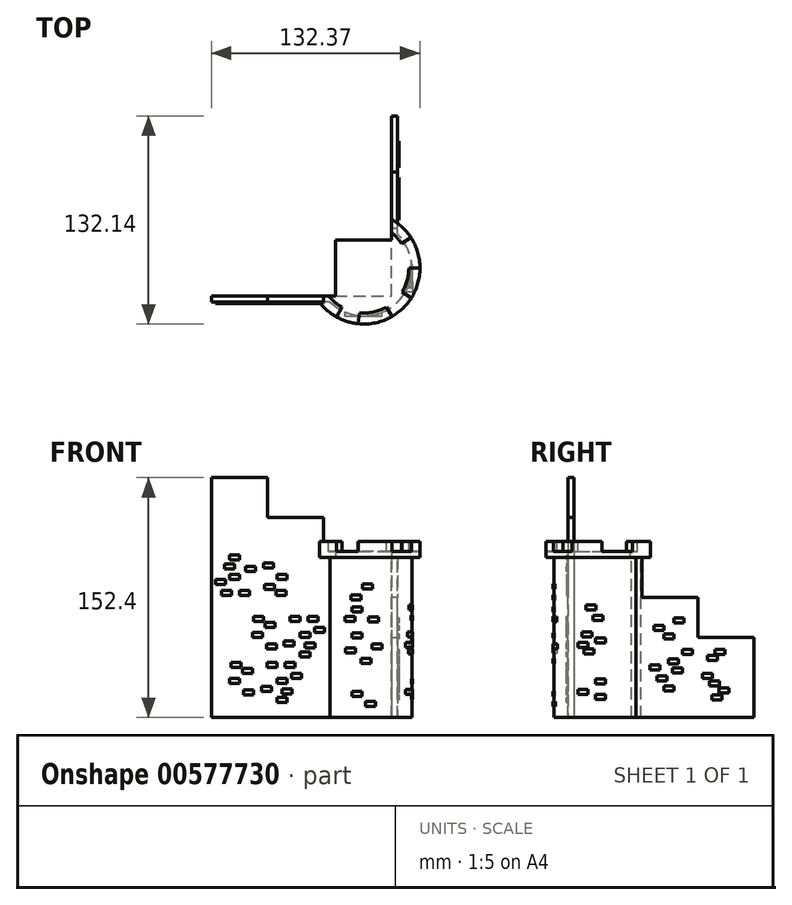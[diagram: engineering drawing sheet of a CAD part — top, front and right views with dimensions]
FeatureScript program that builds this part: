
annotation { "Feature Type Name" : "Feature", "Feature Type Description" : "" }
export const myFeature = defineFeature(function(context is Context, id is Id, definition is map)
    precondition{}
    {
        {
            var Q0;
            Q0=qCreatedBy(makeId("Top.planeOp"),FACE);
            var sketch = newSketch(context, id + "F0", { "sketchPlane" : qUnion([Q0])});
            skLineSegment(sketch, "E0.bottom", {"start": v(-57.15, -57.15) * mm, "end": v(57.15, -57.15) * mm});
            skLineSegment(sketch, "E0.top", {"start": v(-57.15, 57.15) * mm, "end": v(57.15, 57.15) * mm});
            skLineSegment(sketch, "E0.left", {"start": v(-57.15, -57.15) * mm, "end": v(-57.15, 57.15) * mm});
            skLineSegment(sketch, "E0.right", {"start": v(57.15, -57.15) * mm, "end": v(57.15, 57.15) * mm});
            skPoint(sketch, "E0.middle", {"position": v(0, 0) * mm});
            skLineSegment(sketch, "E1.bottom", {"start": v(57.15, -57.15) * mm, "end": v(21.6, -57.15) * mm});
            skLineSegment(sketch, "E1.top", {"start": v(57.15, -21.59) * mm, "end": v(21.59, -21.6) * mm});
            skLineSegment(sketch, "E1.left", {"start": v(57.15, -57.15) * mm, "end": v(57.15, -21.59) * mm});
            skLineSegment(sketch, "E1.right", {"start": v(21.6, -57.15) * mm, "end": v(21.59, -21.6) * mm});
            skLineSegment(sketch, "E2.bottom", {"start": v(57.15, -57.15) * mm, "end": v(39.37, -57.15) * mm});
            skLineSegment(sketch, "E2.top", {"start": v(57.15, -39.37) * mm, "end": v(39.37, -39.37) * mm});
            skLineSegment(sketch, "E2.left", {"start": v(57.15, -57.15) * mm, "end": v(57.15, -39.37) * mm});
            skLineSegment(sketch, "E2.right", {"start": v(39.37, -57.15) * mm, "end": v(39.37, -39.37) * mm});
            skSolve(sketch);
        }
        {
            var Q0;
            Q0=qCreatedBy(makeId("Top.planeOp"),FACE);
            var sketch = newSketch(context, id + "F1", { "sketchPlane" : qUnion([Q0])});
            skLineSegment(sketch, "E3.bottom", {"start": v(57.14, -57.15) * mm, "end": v(-57.16, -57.15) * mm});
            skLineSegment(sketch, "E3.top", {"start": v(57.14, -60.96) * mm, "end": v(-57.16, -60.96) * mm});
            skLineSegment(sketch, "E3.left", {"start": v(57.14, -57.15) * mm, "end": v(57.14, -60.96) * mm});
            skLineSegment(sketch, "E3.right", {"start": v(-57.16, -57.15) * mm, "end": v(-57.16, -60.96) * mm});
            skLineSegment(sketch, "E4.bottom", {"start": v(57.14, -60.96) * mm, "end": v(60.95, -60.96) * mm});
            skLineSegment(sketch, "E4.top", {"start": v(57.14, 57.15) * mm, "end": v(60.95, 57.15) * mm});
            skLineSegment(sketch, "E4.left", {"start": v(57.14, -60.96) * mm, "end": v(57.14, 57.15) * mm});
            skLineSegment(sketch, "E4.right", {"start": v(60.95, -60.96) * mm, "end": v(60.95, 57.15) * mm});
            skSolve(sketch);
        }
        {
            var Q0;
            Q0=qSketchRegion(id+"F1",true);
            extrude(context, id + "F2", {"entities" : qUnion([Q0]), "depth" : 152.4 * mm, "offsetDistance" : 25.4 * mm});
        }
        {
            var Q0;
            Q0=makeQuery(id+"F2.opExtrude","CAP_FACE",FACE,{"disambiguationData":[OSD([sQuery(id+"F1.wireOp",EDGE,"E3.bottom"),sQuery(id+"F1.wireOp",EDGE,"E3.top"),sQuery(id+"F1.wireOp",EDGE,"E3.right"),sQuery(id+"F1.wireOp",EDGE,"E4.bottom"),sQuery(id+"F1.wireOp",EDGE,"E4.top"),sQuery(id+"F1.wireOp",EDGE,"E4.left"),sQuery(id+"F1.wireOp",EDGE,"E4.right")])],"isStart":false});
            var sketch = newSketch(context, id + "F3", { "sketchPlane" : qUnion([Q0])});
            skLineSegment(sketch, "E5.bottom", {"start": v(-57.16, -60.96) * mm, "end": v(-21.56, -60.96) * mm});
            skLineSegment(sketch, "E5.top", {"start": v(-57.16, -57.15) * mm, "end": v(-21.56, -57.15) * mm});
            skLineSegment(sketch, "E5.left", {"start": v(-57.16, -60.96) * mm, "end": v(-57.16, -57.15) * mm});
            skLineSegment(sketch, "E5.right", {"start": v(-21.56, -60.96) * mm, "end": v(-21.56, -57.15) * mm});
            skSolve(sketch);
        }
        {
            var Q0;
            {var subQ2=sQuery(id+"F3.wireOp",EDGE,"E5.right");Q0=makeQuery(id+"F3.imprint","IMPRINT",FACE,{"disambiguationData":[TD([[makeQuery(id+"F3.imprint","IMPRINT",EDGE,{"derivedFrom":subQ2}),-1.0]])]});}
            var sketch = newSketch(context, id + "F4", { "sketchPlane" : qUnion([Q0])});
            skLineSegment(sketch, "E6.bottom", {"start": v(-21.56, -60.96) * mm, "end": v(13.98, -60.96) * mm});
            skLineSegment(sketch, "E6.top", {"start": v(-21.56, -57.15) * mm, "end": v(13.98, -57.15) * mm});
            skLineSegment(sketch, "E6.left", {"start": v(-21.56, -60.96) * mm, "end": v(-21.56, -57.15) * mm});
            skLineSegment(sketch, "E6.right", {"start": v(13.98, -60.96) * mm, "end": v(13.98, -57.15) * mm});
            skSolve(sketch);
        }
        {
            var Q0;
            {var subQ2=sQuery(id+"F3.wireOp",EDGE,"E5.right");Q0=makeQuery(id+"F3.imprint","IMPRINT",FACE,{"disambiguationData":[TD([[makeQuery(id+"F3.imprint","IMPRINT",EDGE,{"derivedFrom":subQ2}),-1.0]])]});}
            var sketch = newSketch(context, id + "F5", { "sketchPlane" : qUnion([Q0])});
            skLineSegment(sketch, "E7.bottom", {"start": v(60.94, 57.16) * mm, "end": v(57.04, 57.16) * mm});
            skLineSegment(sketch, "E7.top", {"start": v(60.94, 21.5) * mm, "end": v(57.04, 21.5) * mm});
            skLineSegment(sketch, "E7.left", {"start": v(60.94, 57.16) * mm, "end": v(60.94, 21.5) * mm});
            skLineSegment(sketch, "E7.right", {"start": v(57.04, 57.16) * mm, "end": v(57.04, 21.5) * mm});
            skSolve(sketch);
        }
        {
            var Q0;
            {var subQ2=sQuery(id+"F3.wireOp",EDGE,"E5.right");Q0=makeQuery(id+"F3.imprint","IMPRINT",FACE,{"disambiguationData":[TD([[makeQuery(id+"F3.imprint","IMPRINT",EDGE,{"derivedFrom":subQ2}),-1.0]])]});}
            var sketch = newSketch(context, id + "F6", { "sketchPlane" : qUnion([Q0])});
            skLineSegment(sketch, "E8.bottom", {"start": v(61.03, 21.57) * mm, "end": v(56.87, 21.57) * mm});
            skLineSegment(sketch, "E8.top", {"start": v(61.03, -14) * mm, "end": v(56.87, -14) * mm});
            skLineSegment(sketch, "E8.left", {"start": v(61.03, 21.57) * mm, "end": v(61.03, -14) * mm});
            skLineSegment(sketch, "E8.right", {"start": v(56.87, 21.57) * mm, "end": v(56.87, -14) * mm});
            skSolve(sketch);
        }
        {
            var Q0;
            Q0=qSketchRegion(id+"F4",true);
            extrude(context, id + "F7", {"entities" : qUnion([Q0]), "operationType" : NewBodyOperationType.REMOVE, "oppositeDirection" : true, "depth" : 25.4 * mm, "offsetDistance" : 25.4 * mm});
        }
        {
            var Q0;
            Q0=qSketchRegion(id+"F6",true);
            extrude(context, id + "F8", {"entities" : qUnion([Q0]), "operationType" : NewBodyOperationType.REMOVE, "oppositeDirection" : true, "depth" : 76.2 * mm, "offsetDistance" : 25.4 * mm});
        }
        {
            var Q0;
            {var subQ2=sQuery(id+"F3.wireOp",EDGE,"E5.right");Q0=makeQuery(id+"F3.imprint","IMPRINT",FACE,{"disambiguationData":[TD([[makeQuery(id+"F3.imprint","IMPRINT",EDGE,{"derivedFrom":subQ2}),-1.0]])]});}
            var sketch = newSketch(context, id + "F9", { "sketchPlane" : qUnion([Q0])});
            skLineSegment(sketch, "E9.bottom", {"start": v(13.92, -61.53) * mm, "end": v(78.38, -61.53) * mm});
            skLineSegment(sketch, "E9.top", {"start": v(13.92, -13.89) * mm, "end": v(78.38, -13.89) * mm});
            skLineSegment(sketch, "E9.left", {"start": v(13.92, -61.53) * mm, "end": v(13.92, -13.89) * mm});
            skLineSegment(sketch, "E9.right", {"start": v(78.38, -61.53) * mm, "end": v(78.38, -13.89) * mm});
            skSolve(sketch);
        }
        {
            var Q0;
            Q0=qSketchRegion(id+"F9",true);
            extrude(context, id + "F10", {"entities" : qUnion([Q0]), "operationType" : NewBodyOperationType.REMOVE, "oppositeDirection" : true, "depth" : 50.8 * mm, "offsetDistance" : 25.4 * mm});
        }
        {
            var Q0;
            Q0=makeQuery(id+"F10.boolean.opBoolean","COPY",FACE,{"derivedFrom":makeQuery(id+"F10.opExtrude","CAP_FACE",FACE,{"disambiguationData":[OSD([sQuery(id+"F9.wireOp",EDGE,"E9.bottom"),sQuery(id+"F9.wireOp",EDGE,"E9.top"),sQuery(id+"F9.wireOp",EDGE,"E9.left"),sQuery(id+"F9.wireOp",EDGE,"E9.right")])],"isStart":false})});
            var sketch = newSketch(context, id + "F11", { "sketchPlane" : qUnion([Q0])});
            skCircle(sketch, "E10", {"center": v(39.65, -39.43) * mm, "radius": 35.56 * mm});
            skSolve(sketch);
        }
        {
            var Q0;
            Q0=qSketchRegion(id+"F11",true);
            extrude(context, id + "F12", {"entities" : qUnion([Q0]), "operationType" : NewBodyOperationType.ADD, "depth" : 10.16 * mm, "offsetDistance" : 25.4 * mm});
        }
        {
            var Q0;
            Q0=qSketchRegion(id+"F5",true);
            extrude(context, id + "F13", {"entities" : qUnion([Q0]), "operationType" : NewBodyOperationType.REMOVE, "oppositeDirection" : true, "depth" : 101.6 * mm, "offsetDistance" : 25.4 * mm});
        }
        {
            var Q0;
            Q0=makeQuery(id+"F12.opExtrude","CAP_FACE",FACE,{"disambiguationData":[OSD([sQuery(id+"F11.wireOp",EDGE,"E10")])],"isStart":true});
            var sketch = newSketch(context, id + "F14", { "sketchPlane" : qUnion([Q0])});
            skCircle(sketch, "E11", {"center": v(39.65, 39.43) * mm, "radius": 30.4 * mm});
            skSolve(sketch);
        }
        {
            var Q0;
            Q0=qSketchRegion(id+"F14",true);
            extrude(context, id + "F15", {"entities" : qUnion([Q0]), "operationType" : NewBodyOperationType.ADD, "depth" : 101.6 * mm, "offsetDistance" : 25.4 * mm});
        }
        {
            var Q0;
            Q0=makeQuery(id+"F2.opExtrude","SWEPT_FACE",FACE,{"disambiguationData":[OSD([sQuery(id+"F1.wireOp",EDGE,"E3.top"),sQuery(id+"F1.wireOp",EDGE,"E4.bottom")])]});
            var sketch = newSketch(context, id + "F16", { "sketchPlane" : qUnion([Q0])});
            skLineSegment(sketch, "E12.bottom", {"start": v(-45.66, 21.63) * mm, "end": v(-39.31, 21.63) * mm});
            skLineSegment(sketch, "E12.top", {"start": v(-45.66, 24.8) * mm, "end": v(-39.31, 24.8) * mm});
            skLineSegment(sketch, "E12.left", {"start": v(-45.66, 21.63) * mm, "end": v(-45.66, 24.8) * mm});
            skLineSegment(sketch, "E12.right", {"start": v(-39.31, 21.63) * mm, "end": v(-39.31, 24.8) * mm});
            skLineSegment(sketch, "E13.bottom", {"start": v(-6.35, 24.8) * mm, "end": v(0, 24.8) * mm});
            skLineSegment(sketch, "E13.top", {"start": v(-6.35, 27.98) * mm, "end": v(0, 27.98) * mm});
            skLineSegment(sketch, "E13.left", {"start": v(-6.35, 24.8) * mm, "end": v(-6.35, 27.98) * mm});
            skLineSegment(sketch, "E13.right", {"start": v(0, 24.8) * mm, "end": v(0, 27.98) * mm});
            skLineSegment(sketch, "E14.bottom", {"start": v(-25.42, 19.65) * mm, "end": v(-19.07, 19.65) * mm});
            skLineSegment(sketch, "E14.top", {"start": v(-25.42, 16.47) * mm, "end": v(-19.07, 16.47) * mm});
            skLineSegment(sketch, "E14.left", {"start": v(-25.42, 19.65) * mm, "end": v(-25.42, 16.47) * mm});
            skLineSegment(sketch, "E14.right", {"start": v(-19.07, 19.65) * mm, "end": v(-19.07, 16.47) * mm});
            skLineSegment(sketch, "E15.bottom", {"start": v(-38.5, 31.94) * mm, "end": v(-44.85, 31.94) * mm});
            skLineSegment(sketch, "E15.top", {"start": v(-38.5, 35.11) * mm, "end": v(-44.85, 35.11) * mm});
            skLineSegment(sketch, "E15.left", {"start": v(-38.5, 31.94) * mm, "end": v(-38.5, 35.11) * mm});
            skLineSegment(sketch, "E15.right", {"start": v(-44.85, 31.94) * mm, "end": v(-44.85, 35.11) * mm});
            skLineSegment(sketch, "E16.bottom", {"start": v(-31.2, 27.98) * mm, "end": v(-37.54, 27.98) * mm});
            skLineSegment(sketch, "E16.top", {"start": v(-31.2, 31.15) * mm, "end": v(-37.54, 31.15) * mm});
            skLineSegment(sketch, "E16.left", {"start": v(-31.2, 27.98) * mm, "end": v(-31.2, 31.15) * mm});
            skLineSegment(sketch, "E16.right", {"start": v(-37.54, 27.98) * mm, "end": v(-37.54, 31.15) * mm});
            skLineSegment(sketch, "E17.bottom", {"start": v(-10.36, 31.94) * mm, "end": v(-4, 31.94) * mm});
            skLineSegment(sketch, "E17.top", {"start": v(-10.36, 35.11) * mm, "end": v(-4, 35.11) * mm});
            skLineSegment(sketch, "E17.left", {"start": v(-10.36, 31.94) * mm, "end": v(-10.36, 35.11) * mm});
            skLineSegment(sketch, "E17.right", {"start": v(-4, 31.94) * mm, "end": v(-4, 35.11) * mm});
            skLineSegment(sketch, "E18.bottom", {"start": v(-30.45, 14.43) * mm, "end": v(-36.8, 14.43) * mm});
            skLineSegment(sketch, "E18.top", {"start": v(-30.45, 17.6) * mm, "end": v(-36.8, 17.6) * mm});
            skLineSegment(sketch, "E18.left", {"start": v(-30.45, 14.43) * mm, "end": v(-30.45, 17.6) * mm});
            skLineSegment(sketch, "E18.right", {"start": v(-36.8, 14.43) * mm, "end": v(-36.8, 17.6) * mm});
            skLineSegment(sketch, "E19.bottom", {"start": v(-15.4, 9.44) * mm, "end": v(-9.05, 9.44) * mm});
            skLineSegment(sketch, "E19.top", {"start": v(-15.4, 12.62) * mm, "end": v(-9.05, 12.62) * mm});
            skLineSegment(sketch, "E19.left", {"start": v(-15.4, 9.44) * mm, "end": v(-15.4, 12.62) * mm});
            skLineSegment(sketch, "E19.right", {"start": v(-9.05, 9.44) * mm, "end": v(-9.05, 12.62) * mm});
            skLineSegment(sketch, "E20.bottom", {"start": v(-12.27, 15.05) * mm, "end": v(-5.92, 15.05) * mm});
            skLineSegment(sketch, "E20.top", {"start": v(-12.27, 18.22) * mm, "end": v(-5.92, 18.22) * mm});
            skLineSegment(sketch, "E20.left", {"start": v(-12.27, 15.05) * mm, "end": v(-12.27, 18.22) * mm});
            skLineSegment(sketch, "E20.right", {"start": v(-5.92, 15.05) * mm, "end": v(-5.92, 18.22) * mm});
            skPoint(sketch, "E21.firstSnap0", {"position": v(-9.1, 15.05) * mm});
            skLineSegment(sketch, "E21.bottom", {"start": v(-9.1, 21.63) * mm, "end": v(-15.44, 21.63) * mm});
            skLineSegment(sketch, "E21.top", {"start": v(-9.1, 24.8) * mm, "end": v(-15.44, 24.8) * mm});
            skLineSegment(sketch, "E21.left", {"start": v(-9.1, 21.63) * mm, "end": v(-9.1, 24.8) * mm});
            skLineSegment(sketch, "E21.right", {"start": v(-15.44, 21.63) * mm, "end": v(-15.44, 24.8) * mm});
            skLineSegment(sketch, "E22.bottom", {"start": v(-15.44, 31.94) * mm, "end": v(-21.8, 31.94) * mm});
            skLineSegment(sketch, "E22.top", {"start": v(-15.44, 35.11) * mm, "end": v(-21.8, 35.11) * mm});
            skLineSegment(sketch, "E22.left", {"start": v(-15.44, 31.94) * mm, "end": v(-15.44, 35.11) * mm});
            skLineSegment(sketch, "E22.right", {"start": v(-21.8, 31.94) * mm, "end": v(-21.8, 35.11) * mm});
            skLineSegment(sketch, "E23.bottom", {"start": v(-31.2, 50.73) * mm, "end": v(-24.84, 50.73) * mm});
            skLineSegment(sketch, "E23.top", {"start": v(-31.2, 53.9) * mm, "end": v(-24.84, 53.9) * mm});
            skLineSegment(sketch, "E23.left", {"start": v(-31.2, 50.73) * mm, "end": v(-31.2, 53.9) * mm});
            skLineSegment(sketch, "E23.right", {"start": v(-24.84, 50.73) * mm, "end": v(-24.84, 53.9) * mm});
            skLineSegment(sketch, "E24.bottom", {"start": v(8.12, 53.9) * mm, "end": v(14.47, 53.9) * mm});
            skLineSegment(sketch, "E24.top", {"start": v(8.12, 57.08) * mm, "end": v(14.47, 57.08) * mm});
            skLineSegment(sketch, "E24.left", {"start": v(8.12, 53.9) * mm, "end": v(8.12, 57.08) * mm});
            skLineSegment(sketch, "E24.right", {"start": v(14.47, 53.9) * mm, "end": v(14.47, 57.08) * mm});
            skLineSegment(sketch, "E25.bottom", {"start": v(-10.95, 48.75) * mm, "end": v(-4.6, 48.75) * mm});
            skLineSegment(sketch, "E25.top", {"start": v(-10.95, 45.57) * mm, "end": v(-4.6, 45.57) * mm});
            skLineSegment(sketch, "E25.left", {"start": v(-10.95, 48.75) * mm, "end": v(-10.95, 45.57) * mm});
            skLineSegment(sketch, "E25.right", {"start": v(-4.6, 48.75) * mm, "end": v(-4.6, 45.57) * mm});
            skLineSegment(sketch, "E26.bottom", {"start": v(-24.03, 61.04) * mm, "end": v(-30.38, 61.04) * mm});
            skLineSegment(sketch, "E26.top", {"start": v(-24.03, 64.21) * mm, "end": v(-30.38, 64.21) * mm});
            skLineSegment(sketch, "E26.left", {"start": v(-24.03, 61.04) * mm, "end": v(-24.03, 64.21) * mm});
            skLineSegment(sketch, "E26.right", {"start": v(-30.38, 61.04) * mm, "end": v(-30.38, 64.21) * mm});
            skLineSegment(sketch, "E27.bottom", {"start": v(-16.72, 57.08) * mm, "end": v(-23.07, 57.08) * mm});
            skLineSegment(sketch, "E27.top", {"start": v(-16.72, 60.25) * mm, "end": v(-23.07, 60.25) * mm});
            skLineSegment(sketch, "E27.left", {"start": v(-16.72, 57.08) * mm, "end": v(-16.72, 60.25) * mm});
            skLineSegment(sketch, "E27.right", {"start": v(-23.07, 57.08) * mm, "end": v(-23.07, 60.25) * mm});
            skLineSegment(sketch, "E28.bottom", {"start": v(4.11, 61.04) * mm, "end": v(10.46, 61.04) * mm});
            skLineSegment(sketch, "E28.top", {"start": v(4.11, 64.21) * mm, "end": v(10.46, 64.21) * mm});
            skLineSegment(sketch, "E28.left", {"start": v(4.11, 61.04) * mm, "end": v(4.11, 64.21) * mm});
            skLineSegment(sketch, "E28.right", {"start": v(10.46, 61.04) * mm, "end": v(10.46, 64.21) * mm});
            skLineSegment(sketch, "E29.bottom", {"start": v(-15.98, 43.53) * mm, "end": v(-22.33, 43.53) * mm});
            skLineSegment(sketch, "E29.top", {"start": v(-15.98, 46.7) * mm, "end": v(-22.33, 46.7) * mm});
            skLineSegment(sketch, "E29.left", {"start": v(-15.98, 43.53) * mm, "end": v(-15.98, 46.7) * mm});
            skLineSegment(sketch, "E29.right", {"start": v(-22.33, 43.53) * mm, "end": v(-22.33, 46.7) * mm});
            skLineSegment(sketch, "E30.bottom", {"start": v(-0.93, 38.54) * mm, "end": v(5.42, 38.54) * mm});
            skLineSegment(sketch, "E30.top", {"start": v(-0.93, 41.72) * mm, "end": v(5.42, 41.72) * mm});
            skLineSegment(sketch, "E30.left", {"start": v(-0.93, 38.54) * mm, "end": v(-0.93, 41.72) * mm});
            skLineSegment(sketch, "E30.right", {"start": v(5.42, 38.54) * mm, "end": v(5.42, 41.72) * mm});
            skLineSegment(sketch, "E31.bottom", {"start": v(2.2, 44.15) * mm, "end": v(8.55, 44.15) * mm});
            skLineSegment(sketch, "E31.top", {"start": v(2.2, 47.32) * mm, "end": v(8.55, 47.32) * mm});
            skLineSegment(sketch, "E31.left", {"start": v(2.2, 44.15) * mm, "end": v(2.2, 47.32) * mm});
            skLineSegment(sketch, "E31.right", {"start": v(8.55, 44.15) * mm, "end": v(8.55, 47.32) * mm});
            skPoint(sketch, "E32.firstSnap0", {"position": v(5.38, 44.15) * mm});
            skLineSegment(sketch, "E32.bottom", {"start": v(5.38, 50.73) * mm, "end": v(-0.97, 50.73) * mm});
            skLineSegment(sketch, "E32.top", {"start": v(5.38, 53.9) * mm, "end": v(-0.97, 53.9) * mm});
            skLineSegment(sketch, "E32.left", {"start": v(5.38, 50.73) * mm, "end": v(5.38, 53.9) * mm});
            skLineSegment(sketch, "E32.right", {"start": v(-0.97, 50.73) * mm, "end": v(-0.97, 53.9) * mm});
            skLineSegment(sketch, "E33.bottom", {"start": v(-0.97, 61.04) * mm, "end": v(-7.32, 61.04) * mm});
            skLineSegment(sketch, "E33.top", {"start": v(-0.97, 64.21) * mm, "end": v(-7.32, 64.21) * mm});
            skLineSegment(sketch, "E33.left", {"start": v(-0.97, 61.04) * mm, "end": v(-0.97, 64.21) * mm});
            skLineSegment(sketch, "E33.right", {"start": v(-7.32, 61.04) * mm, "end": v(-7.32, 64.21) * mm});
            skLineSegment(sketch, "E34.bottom", {"start": v(-9.05, 90.93) * mm, "end": v(-15.4, 90.93) * mm});
            skLineSegment(sketch, "E34.top", {"start": v(-9.05, 87.76) * mm, "end": v(-15.4, 87.76) * mm});
            skLineSegment(sketch, "E34.left", {"start": v(-9.05, 90.93) * mm, "end": v(-9.05, 87.76) * mm});
            skLineSegment(sketch, "E34.right", {"start": v(-15.4, 90.93) * mm, "end": v(-15.4, 87.76) * mm});
            skLineSegment(sketch, "E35.bottom", {"start": v(-48.36, 87.76) * mm, "end": v(-54.71, 87.76) * mm});
            skLineSegment(sketch, "E35.top", {"start": v(-48.36, 84.58) * mm, "end": v(-54.71, 84.58) * mm});
            skLineSegment(sketch, "E35.left", {"start": v(-48.36, 87.76) * mm, "end": v(-48.36, 84.58) * mm});
            skLineSegment(sketch, "E35.right", {"start": v(-54.71, 87.76) * mm, "end": v(-54.71, 84.58) * mm});
            skLineSegment(sketch, "E36.bottom", {"start": v(-29.3, 92.91) * mm, "end": v(-35.64, 92.91) * mm});
            skLineSegment(sketch, "E36.top", {"start": v(-29.3, 96.09) * mm, "end": v(-35.64, 96.09) * mm});
            skLineSegment(sketch, "E36.left", {"start": v(-29.3, 92.91) * mm, "end": v(-29.3, 96.09) * mm});
            skLineSegment(sketch, "E36.right", {"start": v(-35.64, 92.91) * mm, "end": v(-35.64, 96.09) * mm});
            skLineSegment(sketch, "E37.bottom", {"start": v(-16.22, 80.62) * mm, "end": v(-9.87, 80.62) * mm});
            skLineSegment(sketch, "E37.top", {"start": v(-16.22, 77.45) * mm, "end": v(-9.87, 77.45) * mm});
            skLineSegment(sketch, "E37.left", {"start": v(-16.22, 80.62) * mm, "end": v(-16.22, 77.45) * mm});
            skLineSegment(sketch, "E37.right", {"start": v(-9.87, 80.62) * mm, "end": v(-9.87, 77.45) * mm});
            skLineSegment(sketch, "E38.bottom", {"start": v(-23.52, 84.58) * mm, "end": v(-17.17, 84.58) * mm});
            skLineSegment(sketch, "E38.top", {"start": v(-23.52, 81.4) * mm, "end": v(-17.17, 81.4) * mm});
            skLineSegment(sketch, "E38.left", {"start": v(-23.52, 84.58) * mm, "end": v(-23.52, 81.4) * mm});
            skLineSegment(sketch, "E38.right", {"start": v(-17.17, 84.58) * mm, "end": v(-17.17, 81.4) * mm});
            skLineSegment(sketch, "E39.bottom", {"start": v(-44.36, 80.62) * mm, "end": v(-50.7, 80.62) * mm});
            skLineSegment(sketch, "E39.top", {"start": v(-44.36, 77.45) * mm, "end": v(-50.7, 77.45) * mm});
            skLineSegment(sketch, "E39.left", {"start": v(-44.36, 80.62) * mm, "end": v(-44.36, 77.45) * mm});
            skLineSegment(sketch, "E39.right", {"start": v(-50.7, 80.62) * mm, "end": v(-50.7, 77.45) * mm});
            skLineSegment(sketch, "E40.bottom", {"start": v(-24.27, 98.13) * mm, "end": v(-17.92, 98.13) * mm});
            skLineSegment(sketch, "E40.top", {"start": v(-24.27, 94.95) * mm, "end": v(-17.92, 94.95) * mm});
            skLineSegment(sketch, "E40.left", {"start": v(-24.27, 98.13) * mm, "end": v(-24.27, 94.95) * mm});
            skLineSegment(sketch, "E40.right", {"start": v(-17.92, 98.13) * mm, "end": v(-17.92, 94.95) * mm});
            skLineSegment(sketch, "E41.bottom", {"start": v(-39.31, 103.12) * mm, "end": v(-45.66, 103.12) * mm});
            skLineSegment(sketch, "E41.top", {"start": v(-39.31, 99.94) * mm, "end": v(-45.66, 99.94) * mm});
            skLineSegment(sketch, "E41.left", {"start": v(-39.31, 103.12) * mm, "end": v(-39.31, 99.94) * mm});
            skLineSegment(sketch, "E41.right", {"start": v(-45.66, 103.12) * mm, "end": v(-45.66, 99.94) * mm});
            skLineSegment(sketch, "E42.bottom", {"start": v(-42.45, 97.51) * mm, "end": v(-48.8, 97.51) * mm});
            skLineSegment(sketch, "E42.top", {"start": v(-42.45, 94.34) * mm, "end": v(-48.8, 94.34) * mm});
            skLineSegment(sketch, "E42.left", {"start": v(-42.45, 97.51) * mm, "end": v(-42.45, 94.34) * mm});
            skLineSegment(sketch, "E42.right", {"start": v(-48.8, 97.51) * mm, "end": v(-48.8, 94.34) * mm});
            skPoint(sketch, "E43.firstSnap0", {"position": v(-45.62, 97.51) * mm});
            skLineSegment(sketch, "E43.bottom", {"start": v(-45.62, 90.93) * mm, "end": v(-39.27, 90.93) * mm});
            skLineSegment(sketch, "E43.top", {"start": v(-45.62, 87.76) * mm, "end": v(-39.27, 87.76) * mm});
            skLineSegment(sketch, "E43.left", {"start": v(-45.62, 90.93) * mm, "end": v(-45.62, 87.76) * mm});
            skLineSegment(sketch, "E43.right", {"start": v(-39.27, 90.93) * mm, "end": v(-39.27, 87.76) * mm});
            skLineSegment(sketch, "E44.bottom", {"start": v(-39.27, 80.62) * mm, "end": v(-32.92, 80.62) * mm});
            skLineSegment(sketch, "E44.top", {"start": v(-39.27, 77.45) * mm, "end": v(-32.92, 77.45) * mm});
            skLineSegment(sketch, "E44.left", {"start": v(-39.27, 80.62) * mm, "end": v(-39.27, 77.45) * mm});
            skLineSegment(sketch, "E44.right", {"start": v(-32.92, 80.62) * mm, "end": v(-32.92, 77.45) * mm});
            skSolve(sketch);
        }
        {
            var Q0;
            Q0 = qSketchRegion(id + "F16", true);
            extrude(context, id + "F17", {"entities" : qUnion([Q0]), "operationType" : NewBodyOperationType.ADD, "depth" : 1.02 * mm, "offsetDistance" : 25.4 * mm});
        }
        {
            var Q0;
            Q0=makeQuery(id+"F0.imprint","IMPRINT",FACE,{"disambiguationData":[TD([[makeQuery(id+"F0.imprint","IMPRINT",EDGE,{"derivedFrom":sQuery(id+"F0.wireOp",EDGE,"E0.bottom")}),1.0]])]});
            var sketch = newSketch(context, id + "F18", { "sketchPlane" : qUnion([Q0])});
            skLineSegment(sketch, "E45.bottom", {"start": v(21.56, -57.15) * mm, "end": v(-4.41, -57.15) * mm});
            skLineSegment(sketch, "E45.top", {"start": v(21.56, -19.75) * mm, "end": v(-4.41, -19.75) * mm});
            skLineSegment(sketch, "E45.left", {"start": v(21.56, -57.15) * mm, "end": v(21.56, -19.75) * mm});
            skLineSegment(sketch, "E45.right", {"start": v(-4.41, -57.15) * mm, "end": v(-4.41, -19.75) * mm});
            skLineSegment(sketch, "E46.bottom", {"start": v(57.11, -21.63) * mm, "end": v(3.08, -21.63) * mm});
            skLineSegment(sketch, "E46.top", {"start": v(57.11, 0) * mm, "end": v(3.08, 0) * mm});
            skLineSegment(sketch, "E46.left", {"start": v(57.11, -21.63) * mm, "end": v(57.11, 0) * mm});
            skLineSegment(sketch, "E46.right", {"start": v(3.08, -21.63) * mm, "end": v(3.08, 0) * mm});
            skSolve(sketch);
        }
        {
            var Q0;
            Q0 = qSketchRegion(id + "F18", true);
            extrude(context, id + "F19", {"entities" : qUnion([Q0]), "operationType" : NewBodyOperationType.REMOVE, "depth" : 128.02 * mm, "offsetDistance" : 25.4 * mm});
        }
        {
            var Q0;
            Q0=makeQuery(id+"F0.imprint","IMPRINT",FACE,{"disambiguationData":[TD([[makeQuery(id+"F0.imprint","IMPRINT",EDGE,{"derivedFrom":sQuery(id+"F0.wireOp",EDGE,"E0.bottom")}),1.0]])]});
            var sketch = newSketch(context, id + "F20", { "sketchPlane" : qUnion([Q0])});
            skLineSegment(sketch, "E47.bottom", {"start": v(57.16, -57.15) * mm, "end": v(20.61, -57.15) * mm});
            skLineSegment(sketch, "E47.top", {"start": v(57.16, -20.54) * mm, "end": v(20.61, -20.54) * mm});
            skLineSegment(sketch, "E47.left", {"start": v(57.16, -57.15) * mm, "end": v(57.16, -20.54) * mm});
            skLineSegment(sketch, "E47.right", {"start": v(20.61, -57.15) * mm, "end": v(20.61, -20.54) * mm});
            skSolve(sketch);
        }
        {
            var Q0;
            Q0 = qSketchRegion(id + "F20", true);
            extrude(context, id + "F21", {"entities" : qUnion([Q0]), "operationType" : NewBodyOperationType.REMOVE, "depth" : 101.6 * mm, "offsetDistance" : 25.4 * mm});
        }
        {
            var Q0;
            Q0=makeQuery(id+"F12.opExtrude","CAP_FACE",FACE,{"disambiguationData":[OSD([sQuery(id+"F11.wireOp",EDGE,"E10")])],"isStart":false});
            var sketch = newSketch(context, id + "F22", { "sketchPlane" : qUnion([Q0])});
            skCircle(sketch, "E48", {"center": v(39.65, -39.43) * mm, "radius": 28.54 * mm});
            skSolve(sketch);
        }
        {
            var Q0;
            Q0 = qSketchRegion(id + "F22", true);
            extrude(context, id + "F23", {"entities" : qUnion([Q0]), "operationType" : NewBodyOperationType.REMOVE, "oppositeDirection" : true, "depth" : 6.35 * mm, "offsetDistance" : 25.4 * mm});
        }
        {
            var Q0;
            Q0=makeQuery(id+"F23.boolean.opBoolean","COPY",FACE,{"derivedFrom":makeQuery(id+"F23.opExtrude","CAP_FACE",FACE,{"disambiguationData":[OSD([sQuery(id+"F22.wireOp",EDGE,"E48")])],"isStart":false})});
            var sketch = newSketch(context, id + "F24", { "sketchPlane" : qUnion([Q0])});
            skLineSegment(sketch, "E49", {"start": v(39.65, -39.43) * mm, "end": v(17.27, -79.23) * mm});
            skLineSegment(sketch, "E50", {"start": v(17.27, -79.23) * mm, "end": v(34.91, -85.27) * mm});
            skLineSegment(sketch, "E51", {"start": v(34.91, -85.27) * mm, "end": v(39.65, -39.43) * mm});
            skLineSegment(sketch, "E52", {"start": v(39.65, -39.43) * mm, "end": v(66.28, -85.27) * mm});
            skLineSegment(sketch, "E53", {"start": v(66.28, -85.27) * mm, "end": v(81.82, -66) * mm});
            skLineSegment(sketch, "E54", {"start": v(81.82, -66) * mm, "end": v(39.65, -39.43) * mm});
            skLineSegment(sketch, "E55", {"start": v(39.65, -39.43) * mm, "end": v(93.34, -39.43) * mm});
            skLineSegment(sketch, "E56", {"start": v(93.34, -39.43) * mm, "end": v(78.95, -13.9) * mm});
            skLineSegment(sketch, "E57", {"start": v(78.95, -13.9) * mm, "end": v(39.65, -39.43) * mm});
            skSolve(sketch);
        }
        {
            var Q0;
            Q0 = qSketchRegion(id + "F24", true);
            extrude(context, id + "F25", {"entities" : qUnion([Q0]), "operationType" : NewBodyOperationType.REMOVE, "depth" : 64 * mm, "offsetDistance" : 25.4 * mm});
        }
        {
            var Q0;
            Q0=makeQuery(id+"F21.boolean.opBoolean","COPY",FACE,{"derivedFrom":makeQuery(id+"F21.opExtrude","SWEPT_FACE",FACE,{"disambiguationData":[OSD([sQuery(id+"F20.wireOp",EDGE,"E47.left")])]})});
            var sketch = newSketch(context, id + "F26", { "sketchPlane" : qUnion([Q0])});
            skLineSegment(sketch, "E58.bottom", {"start": v(45, 61.8) * mm, "end": v(38.64, 61.8) * mm});
            skLineSegment(sketch, "E58.top", {"start": v(45, 64.98) * mm, "end": v(38.64, 64.98) * mm});
            skLineSegment(sketch, "E58.left", {"start": v(45, 61.8) * mm, "end": v(45, 64.98) * mm});
            skLineSegment(sketch, "E58.right", {"start": v(38.64, 61.8) * mm, "end": v(38.64, 64.98) * mm});
            skLineSegment(sketch, "E59.bottom", {"start": v(49.38, 68.2) * mm, "end": v(43.03, 68.2) * mm});
            skLineSegment(sketch, "E59.top", {"start": v(49.38, 71.38) * mm, "end": v(43.03, 71.38) * mm});
            skLineSegment(sketch, "E59.left", {"start": v(49.38, 68.2) * mm, "end": v(49.38, 71.38) * mm});
            skLineSegment(sketch, "E59.right", {"start": v(43.03, 68.2) * mm, "end": v(43.03, 71.38) * mm});
            skLineSegment(sketch, "E60.bottom", {"start": v(52, 54.48) * mm, "end": v(45.65, 54.48) * mm});
            skLineSegment(sketch, "E60.top", {"start": v(52, 51.3) * mm, "end": v(45.65, 51.3) * mm});
            skLineSegment(sketch, "E60.left", {"start": v(52, 54.48) * mm, "end": v(52, 51.3) * mm});
            skLineSegment(sketch, "E60.right", {"start": v(45.65, 54.48) * mm, "end": v(45.65, 51.3) * mm});
            skLineSegment(sketch, "E61.bottom", {"start": v(48.26, 47.76) * mm, "end": v(54.6, 47.76) * mm});
            skLineSegment(sketch, "E61.top", {"start": v(48.26, 44.59) * mm, "end": v(54.6, 44.59) * mm});
            skLineSegment(sketch, "E61.left", {"start": v(48.26, 47.76) * mm, "end": v(48.26, 44.59) * mm});
            skLineSegment(sketch, "E61.right", {"start": v(54.6, 47.76) * mm, "end": v(54.6, 44.59) * mm});
            skLineSegment(sketch, "E62.bottom", {"start": v(50.8, 43.7) * mm, "end": v(44.46, 43.7) * mm});
            skLineSegment(sketch, "E62.top", {"start": v(50.8, 40.53) * mm, "end": v(44.46, 40.53) * mm});
            skLineSegment(sketch, "E62.left", {"start": v(50.8, 43.7) * mm, "end": v(50.8, 40.53) * mm});
            skLineSegment(sketch, "E62.right", {"start": v(44.46, 43.7) * mm, "end": v(44.46, 40.53) * mm});
            skLineSegment(sketch, "E63.bottom", {"start": v(43.48, 50.67) * mm, "end": v(37.13, 50.67) * mm});
            skLineSegment(sketch, "E63.top", {"start": v(43.48, 47.5) * mm, "end": v(37.13, 47.5) * mm});
            skLineSegment(sketch, "E63.left", {"start": v(43.48, 50.67) * mm, "end": v(43.48, 47.5) * mm});
            skLineSegment(sketch, "E63.right", {"start": v(37.13, 50.67) * mm, "end": v(37.13, 47.5) * mm});
            skLineSegment(sketch, "E64.bottom", {"start": v(37.13, 24.44) * mm, "end": v(43.48, 24.44) * mm});
            skLineSegment(sketch, "E64.top", {"start": v(37.13, 21.27) * mm, "end": v(43.48, 21.27) * mm});
            skLineSegment(sketch, "E64.left", {"start": v(37.13, 24.44) * mm, "end": v(37.13, 21.27) * mm});
            skLineSegment(sketch, "E64.right", {"start": v(43.48, 24.44) * mm, "end": v(43.48, 21.27) * mm});
            skLineSegment(sketch, "E65.bottom", {"start": v(48.26, 17.9) * mm, "end": v(54.6, 17.9) * mm});
            skLineSegment(sketch, "E65.top", {"start": v(48.26, 14.72) * mm, "end": v(54.6, 14.72) * mm});
            skLineSegment(sketch, "E65.left", {"start": v(48.26, 17.9) * mm, "end": v(48.26, 14.72) * mm});
            skLineSegment(sketch, "E65.right", {"start": v(54.6, 17.9) * mm, "end": v(54.6, 14.72) * mm});
            skLineSegment(sketch, "E66.bottom", {"start": v(37.13, 14.77) * mm, "end": v(43.48, 14.77) * mm});
            skLineSegment(sketch, "E66.top", {"start": v(37.13, 11.6) * mm, "end": v(43.48, 11.6) * mm});
            skLineSegment(sketch, "E66.left", {"start": v(37.13, 14.77) * mm, "end": v(37.13, 11.6) * mm});
            skLineSegment(sketch, "E66.right", {"start": v(43.48, 14.77) * mm, "end": v(43.48, 11.6) * mm});
            skSolve(sketch);
        }
        {
            var Q0;
            Q0 = qSketchRegion(id + "F26", true);
            extrude(context, id + "F27", {"entities" : qUnion([Q0]), "operationType" : NewBodyOperationType.ADD, "oppositeDirection" : true, "depth" : 13.2 * mm, "offsetDistance" : 25.4 * mm});
        }
        {
            var Q0;
            Q0=makeQuery(id+"F21.boolean.opBoolean","COPY",FACE,{"derivedFrom":makeQuery(id+"F21.opExtrude","SWEPT_FACE",FACE,{"disambiguationData":[OSD([sQuery(id+"F20.wireOp",EDGE,"E47.bottom")])]})});
            var sketch = newSketch(context, id + "F28", { "sketchPlane" : qUnion([Q0])});
            skLineSegment(sketch, "E67.bottom", {"start": v(-45.09, 84.91) * mm, "end": v(-38.74, 84.91) * mm});
            skLineSegment(sketch, "E67.top", {"start": v(-45.09, 81.74) * mm, "end": v(-38.74, 81.74) * mm});
            skLineSegment(sketch, "E67.left", {"start": v(-45.09, 84.91) * mm, "end": v(-45.09, 81.74) * mm});
            skLineSegment(sketch, "E67.right", {"start": v(-38.74, 84.91) * mm, "end": v(-38.74, 81.74) * mm});
            skLineSegment(sketch, "E68.bottom", {"start": v(-37.8, 77.97) * mm, "end": v(-31.44, 77.97) * mm});
            skLineSegment(sketch, "E68.top", {"start": v(-37.8, 74.8) * mm, "end": v(-31.44, 74.8) * mm});
            skLineSegment(sketch, "E68.left", {"start": v(-37.8, 77.97) * mm, "end": v(-37.8, 74.8) * mm});
            skLineSegment(sketch, "E68.right", {"start": v(-31.44, 77.97) * mm, "end": v(-31.44, 74.8) * mm});
            skLineSegment(sketch, "E69.bottom", {"start": v(-38.27, 70.2) * mm, "end": v(-31.92, 70.2) * mm});
            skLineSegment(sketch, "E69.top", {"start": v(-38.27, 67.02) * mm, "end": v(-31.92, 67.02) * mm});
            skLineSegment(sketch, "E69.left", {"start": v(-38.27, 70.2) * mm, "end": v(-38.27, 67.02) * mm});
            skLineSegment(sketch, "E69.right", {"start": v(-31.92, 70.2) * mm, "end": v(-31.92, 67.02) * mm});
            skLineSegment(sketch, "E70.bottom", {"start": v(-33.96, 64.22) * mm, "end": v(-27.61, 64.22) * mm});
            skLineSegment(sketch, "E70.top", {"start": v(-33.96, 61.04) * mm, "end": v(-27.61, 61.04) * mm});
            skLineSegment(sketch, "E70.left", {"start": v(-33.96, 64.22) * mm, "end": v(-33.96, 61.04) * mm});
            skLineSegment(sketch, "E70.right", {"start": v(-27.61, 64.22) * mm, "end": v(-27.61, 61.04) * mm});
            skLineSegment(sketch, "E71.bottom", {"start": v(-49.04, 63.98) * mm, "end": v(-42.69, 63.98) * mm});
            skLineSegment(sketch, "E71.top", {"start": v(-49.04, 60.8) * mm, "end": v(-42.69, 60.8) * mm});
            skLineSegment(sketch, "E71.left", {"start": v(-49.04, 63.98) * mm, "end": v(-49.04, 60.8) * mm});
            skLineSegment(sketch, "E71.right", {"start": v(-42.69, 63.98) * mm, "end": v(-42.69, 60.8) * mm});
            skLineSegment(sketch, "E72.bottom", {"start": v(-38.27, 53.7) * mm, "end": v(-31.92, 53.7) * mm});
            skLineSegment(sketch, "E72.top", {"start": v(-38.27, 50.52) * mm, "end": v(-31.92, 50.52) * mm});
            skLineSegment(sketch, "E72.left", {"start": v(-38.27, 53.7) * mm, "end": v(-38.27, 50.52) * mm});
            skLineSegment(sketch, "E72.right", {"start": v(-31.92, 53.7) * mm, "end": v(-31.92, 50.52) * mm});
            skLineSegment(sketch, "E73.bottom", {"start": v(-51.07, 46.88) * mm, "end": v(-44.72, 46.88) * mm});
            skLineSegment(sketch, "E73.top", {"start": v(-51.07, 43.7) * mm, "end": v(-44.72, 43.7) * mm});
            skLineSegment(sketch, "E73.left", {"start": v(-51.07, 46.88) * mm, "end": v(-51.07, 43.7) * mm});
            skLineSegment(sketch, "E73.right", {"start": v(-44.72, 46.88) * mm, "end": v(-44.72, 43.7) * mm});
            skLineSegment(sketch, "E74.bottom", {"start": v(-34.44, 44.12) * mm, "end": v(-28.1, 44.12) * mm});
            skLineSegment(sketch, "E74.top", {"start": v(-34.44, 40.95) * mm, "end": v(-28.1, 40.95) * mm});
            skLineSegment(sketch, "E74.left", {"start": v(-34.44, 44.12) * mm, "end": v(-34.44, 40.95) * mm});
            skLineSegment(sketch, "E74.right", {"start": v(-28.1, 44.12) * mm, "end": v(-28.1, 40.95) * mm});
            skLineSegment(sketch, "E75.bottom", {"start": v(-44.14, 37.67) * mm, "end": v(-37.8, 37.67) * mm});
            skLineSegment(sketch, "E75.top", {"start": v(-44.14, 34.5) * mm, "end": v(-37.8, 34.5) * mm});
            skLineSegment(sketch, "E75.left", {"start": v(-44.14, 37.67) * mm, "end": v(-44.14, 34.5) * mm});
            skLineSegment(sketch, "E75.right", {"start": v(-37.8, 37.67) * mm, "end": v(-37.8, 34.5) * mm});
            skLineSegment(sketch, "E76.bottom", {"start": v(-47.1, 10.25) * mm, "end": v(-40.74, 10.25) * mm});
            skLineSegment(sketch, "E76.top", {"start": v(-47.1, 7.07) * mm, "end": v(-40.74, 7.07) * mm});
            skLineSegment(sketch, "E76.left", {"start": v(-47.1, 10.25) * mm, "end": v(-47.1, 7.07) * mm});
            skLineSegment(sketch, "E76.right", {"start": v(-40.74, 10.25) * mm, "end": v(-40.74, 7.07) * mm});
            skLineSegment(sketch, "E77.bottom", {"start": v(-31.92, 13.5) * mm, "end": v(-38.27, 13.5) * mm});
            skLineSegment(sketch, "E77.top", {"start": v(-31.92, 16.67) * mm, "end": v(-38.27, 16.67) * mm});
            skLineSegment(sketch, "E77.left", {"start": v(-31.92, 13.5) * mm, "end": v(-31.92, 16.67) * mm});
            skLineSegment(sketch, "E77.right", {"start": v(-38.27, 13.5) * mm, "end": v(-38.27, 16.67) * mm});
            skSolve(sketch);
        }
        {
            var Q0;
            Q0 = qSketchRegion(id + "F28", true);
            extrude(context, id + "F29", {"entities" : qUnion([Q0]), "operationType" : NewBodyOperationType.ADD, "oppositeDirection" : true, "depth" : 13.2 * mm, "offsetDistance" : 25.4 * mm});
        }
        {
            var Q0;
            Q0=makeQuery(id+"F2.opExtrude","SWEPT_FACE",FACE,{"disambiguationData":[OSD([sQuery(id+"F1.wireOp",EDGE,"E4.right")])]});
            var sketch = newSketch(context, id + "F30", { "sketchPlane" : qUnion([Q0])});
            skLineSegment(sketch, "E78.bottom", {"start": v(-6.35, 58.52) * mm, "end": v(0, 58.52) * mm});
            skLineSegment(sketch, "E78.top", {"start": v(-6.35, 55.35) * mm, "end": v(0, 55.35) * mm});
            skLineSegment(sketch, "E78.left", {"start": v(-6.35, 58.52) * mm, "end": v(-6.35, 55.35) * mm});
            skLineSegment(sketch, "E78.right", {"start": v(0, 58.52) * mm, "end": v(0, 55.35) * mm});
            skLineSegment(sketch, "E79.bottom", {"start": v(-0.15, 53.18) * mm, "end": v(6.2, 53.18) * mm});
            skLineSegment(sketch, "E79.top", {"start": v(-0.15, 50) * mm, "end": v(6.2, 50) * mm});
            skLineSegment(sketch, "E79.left", {"start": v(-0.15, 53.18) * mm, "end": v(-0.15, 50) * mm});
            skLineSegment(sketch, "E79.right", {"start": v(6.2, 53.18) * mm, "end": v(6.2, 50) * mm});
            skLineSegment(sketch, "E80.bottom", {"start": v(6.45, 63.33) * mm, "end": v(12.8, 63.33) * mm});
            skLineSegment(sketch, "E80.top", {"start": v(6.45, 60.16) * mm, "end": v(12.8, 60.16) * mm});
            skLineSegment(sketch, "E80.left", {"start": v(6.45, 63.33) * mm, "end": v(6.45, 60.16) * mm});
            skLineSegment(sketch, "E80.right", {"start": v(12.8, 63.33) * mm, "end": v(12.8, 60.16) * mm});
            skLineSegment(sketch, "E81.bottom", {"start": v(11.7, 43.29) * mm, "end": v(18.05, 43.29) * mm});
            skLineSegment(sketch, "E81.top", {"start": v(11.7, 40.11) * mm, "end": v(18.05, 40.11) * mm});
            skLineSegment(sketch, "E81.left", {"start": v(11.7, 43.29) * mm, "end": v(11.7, 40.11) * mm});
            skLineSegment(sketch, "E81.right", {"start": v(18.05, 43.29) * mm, "end": v(18.05, 40.11) * mm});
            skLineSegment(sketch, "E82.bottom", {"start": v(-9.03, 33.3) * mm, "end": v(-2.68, 33.3) * mm});
            skLineSegment(sketch, "E82.top", {"start": v(-9.03, 30.13) * mm, "end": v(-2.68, 30.13) * mm});
            skLineSegment(sketch, "E82.left", {"start": v(-9.03, 33.3) * mm, "end": v(-9.03, 30.13) * mm});
            skLineSegment(sketch, "E82.right", {"start": v(-2.68, 33.3) * mm, "end": v(-2.68, 30.13) * mm});
            skLineSegment(sketch, "E83.bottom", {"start": v(2.81, 37.28) * mm, "end": v(9.16, 37.28) * mm});
            skLineSegment(sketch, "E83.top", {"start": v(2.81, 34.1) * mm, "end": v(9.16, 34.1) * mm});
            skLineSegment(sketch, "E83.left", {"start": v(2.81, 37.28) * mm, "end": v(2.81, 34.1) * mm});
            skLineSegment(sketch, "E83.right", {"start": v(9.16, 37.28) * mm, "end": v(9.16, 34.1) * mm});
            skLineSegment(sketch, "E84.bottom", {"start": v(-4.53, 26.5) * mm, "end": v(1.82, 26.5) * mm});
            skLineSegment(sketch, "E84.top", {"start": v(-4.53, 23.33) * mm, "end": v(1.82, 23.33) * mm});
            skLineSegment(sketch, "E84.left", {"start": v(-4.53, 26.5) * mm, "end": v(-4.53, 23.33) * mm});
            skLineSegment(sketch, "E84.right", {"start": v(1.82, 26.5) * mm, "end": v(1.82, 23.33) * mm});
            skLineSegment(sketch, "E85.bottom", {"start": v(5.53, 31.54) * mm, "end": v(11.88, 31.54) * mm});
            skLineSegment(sketch, "E85.top", {"start": v(5.53, 28.36) * mm, "end": v(11.88, 28.36) * mm});
            skLineSegment(sketch, "E85.left", {"start": v(5.53, 31.54) * mm, "end": v(5.53, 28.36) * mm});
            skLineSegment(sketch, "E85.right", {"start": v(11.88, 31.54) * mm, "end": v(11.88, 28.36) * mm});
            skLineSegment(sketch, "E86.bottom", {"start": v(-0.1, 20.07) * mm, "end": v(6.24, 20.07) * mm});
            skLineSegment(sketch, "E86.top", {"start": v(-0.1, 16.9) * mm, "end": v(6.24, 16.9) * mm});
            skLineSegment(sketch, "E86.left", {"start": v(-0.1, 20.07) * mm, "end": v(-0.1, 16.9) * mm});
            skLineSegment(sketch, "E86.right", {"start": v(6.24, 20.07) * mm, "end": v(6.24, 16.9) * mm});
            skLineSegment(sketch, "E87.bottom", {"start": v(32.5, 43.29) * mm, "end": v(38.84, 43.29) * mm});
            skLineSegment(sketch, "E87.top", {"start": v(32.5, 40.11) * mm, "end": v(38.84, 40.11) * mm});
            skLineSegment(sketch, "E87.left", {"start": v(32.5, 43.29) * mm, "end": v(32.5, 40.11) * mm});
            skLineSegment(sketch, "E87.right", {"start": v(38.84, 43.29) * mm, "end": v(38.84, 40.11) * mm});
            skLineSegment(sketch, "E88.bottom", {"start": v(34.12, 39.28) * mm, "end": v(27.77, 39.28) * mm});
            skLineSegment(sketch, "E88.top", {"start": v(34.12, 36.1) * mm, "end": v(27.77, 36.1) * mm});
            skLineSegment(sketch, "E88.left", {"start": v(34.12, 39.28) * mm, "end": v(34.12, 36.1) * mm});
            skLineSegment(sketch, "E88.right", {"start": v(27.77, 39.28) * mm, "end": v(27.77, 36.1) * mm});
            skLineSegment(sketch, "E89.bottom", {"start": v(24.54, 28.02) * mm, "end": v(30.89, 28.02) * mm});
            skLineSegment(sketch, "E89.top", {"start": v(24.54, 24.84) * mm, "end": v(30.89, 24.84) * mm});
            skLineSegment(sketch, "E89.left", {"start": v(24.54, 28.02) * mm, "end": v(24.54, 24.84) * mm});
            skLineSegment(sketch, "E89.right", {"start": v(30.89, 28.02) * mm, "end": v(30.89, 24.84) * mm});
            skLineSegment(sketch, "E90.bottom", {"start": v(28.77, 23.33) * mm, "end": v(35.12, 23.33) * mm});
            skLineSegment(sketch, "E90.top", {"start": v(28.77, 20.16) * mm, "end": v(35.12, 20.16) * mm});
            skLineSegment(sketch, "E90.left", {"start": v(28.77, 23.33) * mm, "end": v(28.77, 20.16) * mm});
            skLineSegment(sketch, "E90.right", {"start": v(35.12, 23.33) * mm, "end": v(35.12, 20.16) * mm});
            skLineSegment(sketch, "E91.bottom", {"start": v(34.8, 18.76) * mm, "end": v(41.14, 18.76) * mm});
            skLineSegment(sketch, "E91.top", {"start": v(34.8, 15.59) * mm, "end": v(41.14, 15.59) * mm});
            skLineSegment(sketch, "E91.left", {"start": v(34.8, 18.76) * mm, "end": v(34.8, 15.59) * mm});
            skLineSegment(sketch, "E91.right", {"start": v(41.14, 18.76) * mm, "end": v(41.14, 15.59) * mm});
            skLineSegment(sketch, "E92.bottom", {"start": v(30.47, 14.24) * mm, "end": v(36.82, 14.24) * mm});
            skLineSegment(sketch, "E92.top", {"start": v(30.47, 11.06) * mm, "end": v(36.82, 11.06) * mm});
            skLineSegment(sketch, "E92.left", {"start": v(30.47, 14.24) * mm, "end": v(30.47, 11.06) * mm});
            skLineSegment(sketch, "E92.right", {"start": v(36.82, 14.24) * mm, "end": v(36.82, 11.06) * mm});
            skSolve(sketch);
        }
        {
            var Q0;
            Q0 = qSketchRegion(id + "F30", true);
            extrude(context, id + "F31", {"entities" : qUnion([Q0]), "operationType" : NewBodyOperationType.ADD, "depth" : 1.02 * mm, "offsetDistance" : 25.4 * mm});
        }
    });
